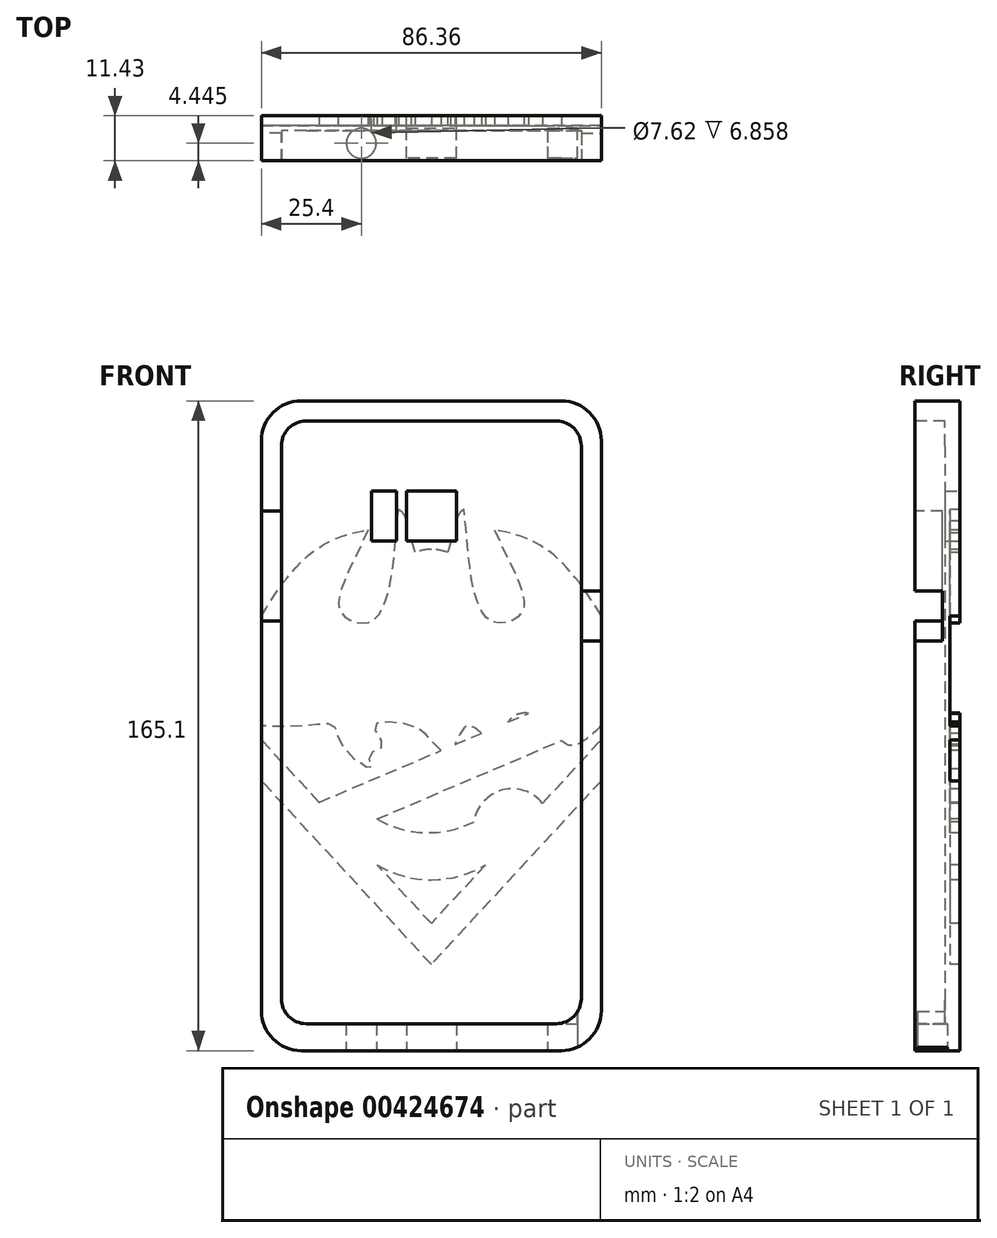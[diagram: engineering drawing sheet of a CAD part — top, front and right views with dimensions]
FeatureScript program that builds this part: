
annotation { "Feature Type Name" : "Feature", "Feature Type Description" : "" }
export const myFeature = defineFeature(function(context is Context, id is Id, definition is map)
    precondition{}
    {
        {
            var Q0;
            Q0=qCreatedBy(makeId("Front.planeOp"),FACE);
            var sketch = newSketch(context, id + "F0", { "sketchPlane" : qUnion([Q0])});
            skLineSegment(sketch, "E0", {"start": v(0, 0) * mm, "end": v(0, -82.55) * mm});
            skLineSegment(sketch, "E1", {"start": v(0, 0) * mm, "end": v(0, 82.55) * mm});
            skLineSegment(sketch, "E2", {"start": v(0, 82.55) * mm, "end": v(-43.18, 82.55) * mm});
            skLineSegment(sketch, "E3", {"start": v(0, 82.55) * mm, "end": v(43.18, 82.55) * mm});
            skLineSegment(sketch, "E4", {"start": v(43.18, 82.55) * mm, "end": v(43.18, -82.55) * mm});
            skLineSegment(sketch, "E5", {"start": v(43.18, -82.55) * mm, "end": v(-43.18, -82.55) * mm});
            skLineSegment(sketch, "E6", {"start": v(-43.18, -82.55) * mm, "end": v(-43.18, 82.55) * mm});
            skSolve(sketch);
        }
        {
            var Q0;
            Q0 = qSketchRegion(id + "F0", true);
            extrude(context, id + "F1", {"entities" : qUnion([Q0]), "depth" : 8.9 * mm});
        }
        {
            var Q0;
            Q0=makeQuery(id+"F1.opExtrude","CAP_FACE",FACE,{"disambiguationData":[OSD([sQuery(id+"F0.wireOp",EDGE,"E2"),sQuery(id+"F0.wireOp",EDGE,"E3"),sQuery(id+"F0.wireOp",EDGE,"E4"),sQuery(id+"F0.wireOp",EDGE,"E5"),sQuery(id+"F0.wireOp",EDGE,"E6")])],"isStart":false});
            var sketch = newSketch(context, id + "F2", { "sketchPlane" : qUnion([Q0])});
            skLineSegment(sketch, "E7", {"start": v(0, 0) * mm, "end": v(0, 77.47) * mm});
            skLineSegment(sketch, "E8", {"start": v(0, 77.47) * mm, "end": v(-38.1, 77.47) * mm});
            skLineSegment(sketch, "E9", {"start": v(-38.1, 77.47) * mm, "end": v(-38.1, -75.7) * mm});
            skLineSegment(sketch, "E10", {"start": v(-38.1, -75.7) * mm, "end": v(38.1, -75.7) * mm});
            skLineSegment(sketch, "E11", {"start": v(38.1, -75.7) * mm, "end": v(38.1, 77.47) * mm});
            skLineSegment(sketch, "E12", {"start": v(38.1, 77.47) * mm, "end": v(0, 77.47) * mm});
            skSolve(sketch);
        }
        {
            var Q0;
            Q0 = qSketchRegion(id + "F2", true);
            extrude(context, id + "F3", {"entities" : qUnion([Q0]), "operationType" : NewBodyOperationType.REMOVE, "oppositeDirection" : true, "depth" : 7.62 * mm});
        }
        {
            var Q0;
            Q0=makeQuery(id+"F1.opExtrude","CAP_FACE",FACE,{"disambiguationData":[OSD([sQuery(id+"F0.wireOp",EDGE,"E2"),sQuery(id+"F0.wireOp",EDGE,"E3"),sQuery(id+"F0.wireOp",EDGE,"E4"),sQuery(id+"F0.wireOp",EDGE,"E5"),sQuery(id+"F0.wireOp",EDGE,"E6")])],"isStart":true});
            var sketch = newSketch(context, id + "F4", { "sketchPlane" : qUnion([Q0])});
            skPoint(sketch, "E13.5.internal.snap0", {"position": v(-43.18, 0) * mm});
            skFitSpline(sketch, "E13", {"points": [v(-43.18, 0) * mm, v(-34.96, -4.96) * mm, v(-28.13, 1.65) * mm, v(-20.27, 1.86) * mm, v(-15.93, -4.14) * mm, v(-9.3, 0) * mm, v(-4.55, -6.62) * mm, v(0, -3.72) * mm, v(4.96, 0) * mm, v(14.48, 0) * mm, v(12.41, -5.17) * mm, v(15.72, -7.45) * mm, v(15.3, -10.76) * mm, v(22.55, -5.17) * mm, v(24.82, 0) * mm, v(32.27, 0) * mm, v(43.18, 0) * mm], "startDerivative": vector(124.68, -118.1) * mm, "endDerivative": vector(115.37, 9.28) * mm});
            skLineSegment(sketch, "E14", {"start": v(-43.18, -13.97) * mm, "end": v(0, -60.61) * mm});
            skLineSegment(sketch, "E15", {"start": v(0, -60.61) * mm, "end": v(43.18, -13.97) * mm});
            skLineSegment(sketch, "E16", {"start": v(-43.18, 0) * mm, "end": v(-43.18, 27.94) * mm});
            skFitSpline(sketch, "E17", {"points": [v(-43.18, 27.94) * mm, v(-16.04, 49.74) * mm], "startDerivative": vector(26.52, 44.64) * mm, "endDerivative": vector(34.13, 4.96) * mm});
            skFitSpline(sketch, "E18", {"points": [v(-16.04, 49.74) * mm, v(-22.64, 28.35) * mm, v(-14.69, 26.9) * mm, v(-8.34, 54.91) * mm], "startDerivative": vector(-48.14, -103.23) * mm, "endDerivative": vector(8.54, 81.55) * mm});
            skFitSpline(sketch, "E19", {"points": [v(-8.34, 54.91) * mm, v(-4.14, 44.06) * mm], "startDerivative": vector(6.87, -1.26) * mm, "endDerivative": vector(4.19, -10.82) * mm});
            skFitSpline(sketch, "E20.MirrorCS", {"points": [v(16.04, 49.74) * mm, v(22.64, 28.35) * mm, v(14.69, 26.9) * mm, v(8.34, 54.91) * mm], "startDerivative": vector(48.14, -103.23) * mm, "endDerivative": vector(-8.54, 81.55) * mm});
            skFitSpline(sketch, "E21.MirrorCS", {"points": [v(43.18, 27.94) * mm, v(16.04, 49.74) * mm], "startDerivative": vector(-26.52, 44.64) * mm, "endDerivative": vector(-34.13, 4.96) * mm});
            skFitSpline(sketch, "E22.MirrorCS", {"points": [v(8.34, 54.91) * mm, v(4.14, 44.06) * mm], "startDerivative": vector(-6.87, -1.26) * mm, "endDerivative": vector(-4.19, -10.82) * mm});
            skArc(sketch, "E23", {"start": v(0, 44.82) * mm, "mid": v(-2.1, 44.6) * mm, "end": v(-4.14, 44.06) * mm});
            skArc(sketch, "E24.MirrorCS", {"start": v(0, 44.82) * mm, "mid": v(2.1, 44.6) * mm, "end": v(4.14, 44.06) * mm});
            skLineSegment(sketch, "E25", {"start": v(-38.06, -9.1) * mm, "end": v(0, -50.22) * mm});
            skLineSegment(sketch, "E26", {"start": v(0, -50.22) * mm, "end": v(13.8, -35.3) * mm});
            skLineSegment(sketch, "E27", {"start": v(-38.06, -9.1) * mm, "end": v(-43.18, -3.58) * mm});
            skArc(sketch, "E28", {"start": v(-13.8, -35.3) * mm, "mid": v(0, -39.14) * mm, "end": v(13.8, -35.3) * mm});
            skArc(sketch, "E29", {"start": v(-10.83, -24.39) * mm, "mid": v(1.58, -27.16) * mm, "end": v(13.8, -23.69) * mm});
            skLineSegment(sketch, "E30", {"start": v(13.8, -23.69) * mm, "end": v(-33.1, -3.76) * mm});
            skLineSegment(sketch, "E31", {"start": v(28.5, -19.44) * mm, "end": v(-2.53, -6.26) * mm});
            skLineSegment(sketch, "E32", {"start": v(-5.97, -4.8) * mm, "end": v(-12.7, -1.94) * mm});
            skLineSegment(sketch, "E33", {"start": v(-19.55, 0.97) * mm, "end": v(-24.66, 3.14) * mm});
            skLineSegment(sketch, "E34", {"start": v(28.5, -19.44) * mm, "end": v(43.18, -3.58) * mm});
            skArc(sketch, "E35", {"start": v(-10.83, -24.39) * mm, "mid": v(-18.01, -16.36) * mm, "end": v(-28.26, -19.7) * mm});
            skSolve(sketch);
        }
        {
            var Q0;
            Q0=makeQuery(id+"F1.opExtrude","SWEPT_FACE",FACE,{"disambiguationData":[OSD([sQuery(id+"F0.wireOp",EDGE,"E5")])]});
            var sketch = newSketch(context, id + "F5", { "sketchPlane" : qUnion([Q0])});
            skLineSegment(sketch, "E36", {"start": v(-43.18, 4.45) * mm, "end": v(-38.1, 4.45) * mm});
            skLineSegment(sketch, "E37", {"start": v(-38.1, 4.45) * mm, "end": v(-38.1, 8.89) * mm});
            skLineSegment(sketch, "E38", {"start": v(-38.1, 8.89) * mm, "end": v(-38.1, 0) * mm});
            skLineSegment(sketch, "E39", {"start": v(43.18, 4.45) * mm, "end": v(38.1, 4.45) * mm});
            skLineSegment(sketch, "E40", {"start": v(38.1, 4.45) * mm, "end": v(38.1, 8.9) * mm});
            skLineSegment(sketch, "E41", {"start": v(38.1, 8.9) * mm, "end": v(38.1, 0) * mm});
            skLineSegment(sketch, "E42", {"start": v(6.35, 4.45) * mm, "end": v(6.35, 0.64) * mm});
            skLineSegment(sketch, "E43", {"start": v(6.35, 4.45) * mm, "end": v(6.35, 8.26) * mm});
            skLineSegment(sketch, "E44", {"start": v(6.35, 8.26) * mm, "end": v(-6.35, 8.26) * mm});
            skLineSegment(sketch, "E45", {"start": v(-6.35, 8.26) * mm, "end": v(-6.35, 0.64) * mm});
            skLineSegment(sketch, "E46", {"start": v(-6.35, 0.64) * mm, "end": v(6.35, 0.64) * mm});
            skCircle(sketch, "E47", {"center": v(-17.78, 4.45) * mm, "radius": 3.81 * mm});
            skLineSegment(sketch, "E48", {"start": v(16.42, 4.45) * mm, "end": v(16.42, 8.26) * mm});
            skLineSegment(sketch, "E49", {"start": v(16.42, 8.26) * mm, "end": v(16.42, 4.45) * mm});
            skLineSegment(sketch, "E50", {"start": v(16.42, 4.45) * mm, "end": v(16.42, 0.64) * mm});
            skLineSegment(sketch, "E51", {"start": v(16.42, 0.64) * mm, "end": v(26.58, 0.64) * mm});
            skLineSegment(sketch, "E52", {"start": v(26.58, 0.64) * mm, "end": v(26.58, 8.26) * mm});
            skLineSegment(sketch, "E53", {"start": v(26.58, 8.26) * mm, "end": v(16.42, 8.26) * mm});
            skLineSegment(sketch, "E54", {"start": v(29.57, 4.45) * mm, "end": v(29.57, 8.26) * mm});
            skLineSegment(sketch, "E55", {"start": v(29.57, 4.45) * mm, "end": v(29.57, 0.64) * mm});
            skLineSegment(sketch, "E56", {"start": v(29.57, 0.64) * mm, "end": v(37.19, 0.64) * mm});
            skLineSegment(sketch, "E57", {"start": v(37.19, 0.64) * mm, "end": v(37.19, 8.26) * mm});
            skLineSegment(sketch, "E58", {"start": v(37.19, 8.26) * mm, "end": v(29.57, 8.26) * mm});
            skLineSegment(sketch, "E59", {"start": v(-38.1, 0) * mm, "end": v(-38.1, 8.9) * mm});
            skLineSegment(sketch, "E60", {"start": v(-38.1, 0) * mm, "end": v(38.1, 0) * mm});
            skSolve(sketch);
        }
        {
            var Q0;
            Q0=makeQuery(id+"F5.imprint","IMPRINT",FACE,{"disambiguationData":[TD([[makeQuery(id+"F5.imprint","IMPRINT",EDGE,{"derivedFrom":sQuery(id+"F5.wireOp",EDGE,"E47")}),1.0]])]});
            var Q1;
            Q1=makeQuery(id+"F5.imprint","IMPRINT",FACE,{"disambiguationData":[TD([[makeQuery(id+"F5.imprint","IMPRINT",EDGE,{"derivedFrom":sQuery(id+"F5.wireOp",EDGE,"E42")}),-1.0]])]});
            var Q2;
            Q2=makeQuery(id+"F5.imprint","IMPRINT",FACE,{"disambiguationData":[TD([[makeQuery(id+"F5.imprint","IMPRINT",EDGE,{"derivedFrom":sQuery(id+"F5.wireOp",EDGE,"E49")}),1.0]])]});
            var Q3;
            Q3=makeQuery(id+"F5.imprint","IMPRINT",FACE,{"disambiguationData":[TD([[makeQuery(id+"F5.imprint","IMPRINT",EDGE,{"derivedFrom":sQuery(id+"F5.wireOp",EDGE,"E54")}),-1.0]])]});
            extrude(context, id + "F6", {"entities" : qUnion([Q0, Q1, Q2, Q3]), "operationType" : NewBodyOperationType.REMOVE, "oppositeDirection" : true, "depth" : 6.86 * mm});
        }
        {
            var Q0;
            Q0=makeQuery(id+"F1.opExtrude","SWEPT_EDGE",EDGE,{"disambiguationData":[OSD([sQuery(id+"F0.wireOp",EDGE,"E5"),sQuery(id+"F0.wireOp",EDGE,"E6")])]});
            var Q1;
            Q1=makeQuery(id+"F1.opExtrude","SWEPT_EDGE",EDGE,{"disambiguationData":[OSD([sQuery(id+"F0.wireOp",EDGE,"E4"),sQuery(id+"F0.wireOp",EDGE,"E5")])]});
            var Q2;
            Q2=makeQuery(id+"F1.opExtrude","SWEPT_EDGE",EDGE,{"disambiguationData":[OSD([sQuery(id+"F0.wireOp",EDGE,"E3"),sQuery(id+"F0.wireOp",EDGE,"E4")])]});
            var Q3;
            Q3=makeQuery(id+"F1.opExtrude","SWEPT_EDGE",EDGE,{"disambiguationData":[OSD([sQuery(id+"F0.wireOp",EDGE,"E2"),sQuery(id+"F0.wireOp",EDGE,"E6")])]});
            fillet(context, id + "F7", {"entities" : qUnion([Q0, Q1, Q2, Q3]), "radius" : 10.16 * mm, "tangentPropagation" : true, "allowEdgeOverflow" : false});
        }
        {
            var Q0;
            Q0=makeQuery(id+"F3.boolean.opBoolean","COPY",EDGE,{"derivedFrom":makeQuery(id+"F3.opExtrude","SWEPT_EDGE",EDGE,{"disambiguationData":[OSD([sQuery(id+"F2.wireOp",EDGE,"E9"),sQuery(id+"F2.wireOp",EDGE,"E10")])]})});
            var Q1;
            Q1=makeQuery(id+"F3.boolean.opBoolean","COPY",EDGE,{"derivedFrom":makeQuery(id+"F3.opExtrude","SWEPT_EDGE",EDGE,{"disambiguationData":[OSD([sQuery(id+"F2.wireOp",EDGE,"E10"),sQuery(id+"F2.wireOp",EDGE,"E11")])]})});
            var Q2;
            Q2=makeQuery(id+"F3.boolean.opBoolean","COPY",EDGE,{"derivedFrom":makeQuery(id+"F3.opExtrude","SWEPT_EDGE",EDGE,{"disambiguationData":[OSD([sQuery(id+"F2.wireOp",EDGE,"E8"),sQuery(id+"F2.wireOp",EDGE,"E9")])]})});
            var Q3;
            Q3=makeQuery(id+"F3.boolean.opBoolean","COPY",EDGE,{"derivedFrom":makeQuery(id+"F3.opExtrude","SWEPT_EDGE",EDGE,{"disambiguationData":[OSD([sQuery(id+"F2.wireOp",EDGE,"E11"),sQuery(id+"F2.wireOp",EDGE,"E12")])]})});
            fillet(context, id + "F8", {"entities" : qUnion([Q0, Q1, Q2, Q3]), "radius" : 6.35 * mm, "tangentPropagation" : true, "allowEdgeOverflow" : false});
        }
        {
            var Q0;
            Q0=makeQuery(id+"F1.opExtrude","SWEPT_FACE",FACE,{"disambiguationData":[OSD([sQuery(id+"F0.wireOp",EDGE,"E4")])]});
            var sketch = newSketch(context, id + "F9", { "sketchPlane" : qUnion([Q0])});
            skLineSegment(sketch, "E61", {"start": v(-4.45, 21.6) * mm, "end": v(-6.99, 21.6) * mm});
            skLineSegment(sketch, "E62", {"start": v(-6.99, 21.6) * mm, "end": v(-6.99, 34.3) * mm});
            skLineSegment(sketch, "E63", {"start": v(-6.99, 34.3) * mm, "end": v(-1.9, 34.3) * mm});
            skLineSegment(sketch, "E64", {"start": v(-1.9, 34.3) * mm, "end": v(-1.9, 21.6) * mm});
            skLineSegment(sketch, "E65", {"start": v(-1.9, 21.6) * mm, "end": v(-4.45, 21.6) * mm});
            skSolve(sketch);
        }
        {
            var Q0;
            Q0=makeQuery(id+"F9.imprint","IMPRINT",FACE,{"disambiguationData":[TD([[makeQuery(id+"F9.imprint","IMPRINT",EDGE,{"derivedFrom":sQuery(id+"F9.wireOp",EDGE,"E61")}),-1.0]])]});
            extrude(context, id + "F10", {"entities" : qUnion([Q0]), "operationType" : NewBodyOperationType.REMOVE, "oppositeDirection" : true, "depth" : 25.4 * mm});
        }
        {
            var Q0;
            Q0=makeQuery(id+"F1.opExtrude","SWEPT_FACE",FACE,{"disambiguationData":[OSD([sQuery(id+"F0.wireOp",EDGE,"E6")])]});
            var sketch = newSketch(context, id + "F11", { "sketchPlane" : qUnion([Q0])});
            skLineSegment(sketch, "E66", {"start": v(4.45, 26.67) * mm, "end": v(1.9, 26.67) * mm});
            skLineSegment(sketch, "E67", {"start": v(1.9, 26.67) * mm, "end": v(1.9, 39.37) * mm});
            skLineSegment(sketch, "E68", {"start": v(1.9, 39.37) * mm, "end": v(6.99, 39.37) * mm});
            skLineSegment(sketch, "E69", {"start": v(6.99, 39.37) * mm, "end": v(6.99, 26.67) * mm});
            skLineSegment(sketch, "E70", {"start": v(6.99, 26.67) * mm, "end": v(4.45, 26.67) * mm});
            skLineSegment(sketch, "E71", {"start": v(4.44, 41.9) * mm, "end": v(1.9, 41.9) * mm});
            skLineSegment(sketch, "E72", {"start": v(1.9, 41.9) * mm, "end": v(1.9, 54.6) * mm});
            skLineSegment(sketch, "E73", {"start": v(1.9, 54.6) * mm, "end": v(6.99, 54.6) * mm});
            skLineSegment(sketch, "E74", {"start": v(6.99, 54.6) * mm, "end": v(6.99, 41.9) * mm});
            skLineSegment(sketch, "E75", {"start": v(6.99, 41.9) * mm, "end": v(4.44, 41.9) * mm});
            skSolve(sketch);
        }
        {
            var Q0;
            Q0 = qSketchRegion(id + "F11", true);
            extrude(context, id + "F12", {"entities" : qUnion([Q0]), "operationType" : NewBodyOperationType.REMOVE, "oppositeDirection" : true, "depth" : 25.4 * mm});
        }
        {
            var Q0;
            {var subQ1=sQuery(id+"F4.wireOp",EDGE,"E17");Q0=makeQuery(id+"F4.imprint","IMPRINT",FACE,{"disambiguationData":[TD([[makeQuery(id+"F4.imprint","IMPRINT",EDGE,{"derivedFrom":subQ1}),1.0]])]});}
            var sketch = newSketch(context, id + "F13", { "sketchPlane" : qUnion([Q0])});
            skLineSegment(sketch, "E76.0", {"start": v(-38.1, 77.47) * mm, "end": v(0, 77.47) * mm});
            skLineSegment(sketch, "E77.0", {"start": v(0, 77.47) * mm, "end": v(38.1, 77.47) * mm});
            skLineSegment(sketch, "E78", {"start": v(0, 77.47) * mm, "end": v(0, 47) * mm});
            skLineSegment(sketch, "E79", {"start": v(0, 47) * mm, "end": v(-6.35, 47) * mm});
            skLineSegment(sketch, "E80", {"start": v(-6.35, 47) * mm, "end": v(-6.35, 59.7) * mm});
            skLineSegment(sketch, "E81", {"start": v(-6.35, 59.7) * mm, "end": v(6.35, 59.7) * mm});
            skLineSegment(sketch, "E82", {"start": v(6.35, 59.7) * mm, "end": v(6.35, 47) * mm});
            skLineSegment(sketch, "E83", {"start": v(6.35, 47) * mm, "end": v(0, 47) * mm});
            skLineSegment(sketch, "E84", {"start": v(8.89, 59.7) * mm, "end": v(15.24, 59.7) * mm});
            skLineSegment(sketch, "E85", {"start": v(15.24, 59.7) * mm, "end": v(15.24, 47) * mm});
            skLineSegment(sketch, "E86", {"start": v(15.24, 47) * mm, "end": v(8.9, 47) * mm});
            skLineSegment(sketch, "E87", {"start": v(8.9, 47) * mm, "end": v(8.89, 59.7) * mm});
            skSolve(sketch);
        }
        {
            var Q0;
            Q0 = qSketchRegion(id + "F13", true);
            extrude(context, id + "F14", {"entities" : qUnion([Q0]), "operationType" : NewBodyOperationType.REMOVE, "oppositeDirection" : true, "depth" : 25.4 * mm});
        }
        {
            var Q0;
            {var subQ1=sQuery(id+"F4.wireOp",EDGE,"E17");Q0=makeQuery(id+"F4.imprint","IMPRINT",FACE,{"disambiguationData":[TD([[makeQuery(id+"F4.imprint","IMPRINT",EDGE,{"derivedFrom":subQ1}),1.0]])]});}
            var Q1;
            {var subQ2=sQuery(id+"F4.wireOp",EDGE,"E14");Q1=makeQuery(id+"F4.imprint","IMPRINT",FACE,{"disambiguationData":[TD([[makeQuery(id+"F4.imprint","IMPRINT",EDGE,{"derivedFrom":subQ2}),-1.0]])]});}
            extrude(context, id + "F15", {"entities" : qUnion([Q0, Q1]), "operationType" : NewBodyOperationType.ADD, "depth" : 2.54 * mm});
        }
        {
            var Q0;
            Q0=makeQuery(id+"F15.opExtrude","SWEPT_EDGE",EDGE,{"disambiguationData":[OSD([sQuery(id+"F0.wireOp",EDGE,"E2"),sQuery(id+"F0.wireOp",EDGE,"E3"),sQuery(id+"F0.wireOp",EDGE,"E4")])]});
            var Q1;
            Q1=makeQuery(id+"F15.opExtrude","SWEPT_EDGE",EDGE,{"disambiguationData":[OSD([sQuery(id+"F0.wireOp",EDGE,"E2"),sQuery(id+"F0.wireOp",EDGE,"E3"),sQuery(id+"F0.wireOp",EDGE,"E6")])]});
            var Q2;
            Q2=makeQuery(id+"F15.opExtrude","SWEPT_EDGE",EDGE,{"disambiguationData":[OSD([sQuery(id+"F0.wireOp",EDGE,"E5"),sQuery(id+"F0.wireOp",EDGE,"E6")])]});
            var Q3;
            Q3=makeQuery(id+"F15.opExtrude","SWEPT_EDGE",EDGE,{"disambiguationData":[OSD([sQuery(id+"F0.wireOp",EDGE,"E4"),sQuery(id+"F0.wireOp",EDGE,"E5")])]});
            fillet(context, id + "F16", {"entities" : qUnion([Q0, Q1, Q2, Q3]), "radius" : 10.16 * mm, "tangentPropagation" : true, "allowEdgeOverflow" : false});
        }
        {
            var Q0;
            {var subQ0=sQuery(id+"F4.wireOp",EDGE,"E27");Q0=makeQuery(id+"F4.imprint","IMPRINT",FACE,{"disambiguationData":[TD([[makeQuery(id+"F4.imprint","IMPRINT",EDGE,{"derivedFrom":subQ0}),-1.0]])]});}
            var Q1;
            {var subQ0=sQuery(id+"F4.wireOp",EDGE,"E26");Q1=makeQuery(id+"F4.imprint","IMPRINT",FACE,{"disambiguationData":[TD([[makeQuery(id+"F4.imprint","IMPRINT",EDGE,{"derivedFrom":subQ0}),1.0]])]});}
            var Q2;
            {var subQ3=sQuery(id+"F4.wireOp",EDGE,"E31");Q2=makeQuery(id+"F4.imprint","IMPRINT",FACE,{"disambiguationData":[TD([[makeQuery(id+"F4.imprint","IMPRINT",EDGE,{"derivedFrom":subQ3}),-1.0]])]});}
            var Q3;
            {var subQ0=sQuery(id+"F4.wireOp",EDGE,"E32");Q3=makeQuery(id+"F4.imprint","IMPRINT",FACE,{"disambiguationData":[TD([[makeQuery(id+"F4.imprint","IMPRINT",EDGE,{"derivedFrom":subQ0}),-1.0]])]});}
            var Q4;
            {var subQ0=sQuery(id+"F4.wireOp",EDGE,"E33");Q4=makeQuery(id+"F4.imprint","IMPRINT",FACE,{"disambiguationData":[TD([[makeQuery(id+"F4.imprint","IMPRINT",EDGE,{"derivedFrom":subQ0}),-1.0]])]});}
            extrude(context, id + "F17", {"entities" : qUnion([Q0, Q1, Q2, Q3, Q4]), "operationType" : NewBodyOperationType.ADD, "depth" : 2.54 * mm});
        }
        {
            var Q0;
            Q0=makeQuery(id+"F15.opExtrude","CAP_FACE",FACE,{"disambiguationData":[OSD([sQuery(id+"F0.wireOp",EDGE,"E2"),sQuery(id+"F0.wireOp",EDGE,"E3"),sQuery(id+"F0.wireOp",EDGE,"E4"),sQuery(id+"F0.wireOp",EDGE,"E6"),sQuery(id+"F4.wireOp",EDGE,"E17"),sQuery(id+"F4.wireOp",EDGE,"E18"),sQuery(id+"F4.wireOp",EDGE,"E19"),sQuery(id+"F4.wireOp",EDGE,"E20.MirrorCS"),sQuery(id+"F4.wireOp",EDGE,"E21.MirrorCS"),sQuery(id+"F4.wireOp",EDGE,"E22.MirrorCS"),sQuery(id+"F4.wireOp",EDGE,"E23"),sQuery(id+"F4.wireOp",EDGE,"E24.MirrorCS")])],"isStart":false});
            var sketch = newSketch(context, id + "F18", { "sketchPlane" : qUnion([Q0])});
            skLineSegment(sketch, "E88.0", {"start": v(0, 47) * mm, "end": v(-6.35, 47) * mm});
            skLineSegment(sketch, "E89.0", {"start": v(6.35, 47) * mm, "end": v(0, 47) * mm});
            skLineSegment(sketch, "E90.0", {"start": v(-6.35, 47) * mm, "end": v(-6.35, 59.7) * mm});
            skLineSegment(sketch, "E91.0", {"start": v(6.35, 59.7) * mm, "end": v(6.35, 47) * mm});
            skLineSegment(sketch, "E92.0", {"start": v(-6.35, 59.7) * mm, "end": v(6.35, 59.7) * mm});
            skLineSegment(sketch, "E93.0", {"start": v(8.9, 47) * mm, "end": v(8.89, 59.7) * mm});
            skLineSegment(sketch, "E94.0", {"start": v(8.89, 59.7) * mm, "end": v(15.24, 59.7) * mm});
            skLineSegment(sketch, "E95.0", {"start": v(15.24, 59.7) * mm, "end": v(15.24, 47) * mm});
            skPoint(sketch, "E96.0", {"position": v(12.07, 47) * mm});
            skLineSegment(sketch, "E97.0", {"start": v(15.24, 47) * mm, "end": v(8.9, 47) * mm});
            skSolve(sketch);
        }
        {
            var Q0;
            {var subQ0=sQuery(id+"F18.wireOp",EDGE,"E92.0");Q0=makeQuery(id+"F18.imprint","IMPRINT",FACE,{"disambiguationData":[TD([[makeQuery(id+"F18.imprint","IMPRINT",EDGE,{"derivedFrom":subQ0}),-1.0]])]});}
            var Q1;
            {var subQ4=sQuery(id+"F18.wireOp",EDGE,"E94.0");Q1=makeQuery(id+"F18.imprint","IMPRINT",FACE,{"disambiguationData":[TD([[makeQuery(id+"F18.imprint","IMPRINT",EDGE,{"derivedFrom":subQ4}),-1.0]])]});}
            extrude(context, id + "F19", {"entities" : qUnion([Q0, Q1]), "operationType" : NewBodyOperationType.REMOVE, "endBound" : BoundingType.THROUGH_ALL, "oppositeDirection" : true, "depth" : 25.4 * mm});
        }
        {
            var Q0;
            Q0=makeQuery(id+"F9.imprint","IMPRINT",FACE,{"disambiguationData":[TD([[makeQuery(id+"F9.imprint","IMPRINT",EDGE,{"derivedFrom":sQuery(id+"F9.wireOp",EDGE,"E61")}),1.0]])]});
            var sketch = newSketch(context, id + "F20", { "sketchPlane" : qUnion([Q0])});
            skLineSegment(sketch, "E98.0", {"start": v(-6.99, 21.6) * mm, "end": v(-6.99, 34.3) * mm});
            skLineSegment(sketch, "E99", {"start": v(-6.99, 21.6) * mm, "end": v(-9.5, 21.6) * mm});
            skLineSegment(sketch, "E100", {"start": v(-9.5, 21.6) * mm, "end": v(-9.5, 34.3) * mm});
            skLineSegment(sketch, "E101", {"start": v(-9.5, 34.3) * mm, "end": v(-6.99, 34.3) * mm});
            skSolve(sketch);
        }
        {
            var Q0;
            Q0 = qSketchRegion(id + "F20", true);
            extrude(context, id + "F21", {"entities" : qUnion([Q0]), "operationType" : NewBodyOperationType.REMOVE, "oppositeDirection" : true, "depth" : 12.7 * mm});
        }
        {
            var Q0;
            Q0=makeQuery(id+"F11.imprint","IMPRINT",FACE,{"disambiguationData":[TD([[makeQuery(id+"F11.imprint","IMPRINT",EDGE,{"derivedFrom":sQuery(id+"F11.wireOp",EDGE,"E66")}),1.0]])]});
            var sketch = newSketch(context, id + "F22", { "sketchPlane" : qUnion([Q0])});
            skLineSegment(sketch, "E102.0", {"start": v(6.99, 39.37) * mm, "end": v(6.99, 26.67) * mm});
            skLineSegment(sketch, "E103.0", {"start": v(6.99, 54.6) * mm, "end": v(6.99, 41.9) * mm});
            skLineSegment(sketch, "E104", {"start": v(6.99, 54.6) * mm, "end": v(11.18, 54.6) * mm});
            skLineSegment(sketch, "E105", {"start": v(11.18, 54.6) * mm, "end": v(11.18, 26.67) * mm});
            skLineSegment(sketch, "E106", {"start": v(11.18, 26.67) * mm, "end": v(6.99, 26.67) * mm});
            skLineSegment(sketch, "E107", {"start": v(6.99, 39.37) * mm, "end": v(6.99, 41.9) * mm});
            skSolve(sketch);
        }
        {
            var Q0;
            Q0 = qSketchRegion(id + "F22", true);
            extrude(context, id + "F23", {"entities" : qUnion([Q0]), "operationType" : NewBodyOperationType.REMOVE, "oppositeDirection" : true, "depth" : 12.7 * mm});
        }
        {
            var Q0;
            Q0=makeQuery(id+"F11.imprint","IMPRINT",FACE,{"disambiguationData":[TD([[makeQuery(id+"F11.imprint","IMPRINT",EDGE,{"derivedFrom":sQuery(id+"F11.wireOp",EDGE,"E66")}),1.0]])]});
            var sketch = newSketch(context, id + "F24", { "sketchPlane" : qUnion([Q0])});
            skLineSegment(sketch, "E108.0", {"start": v(1.9, 39.37) * mm, "end": v(6.99, 39.37) * mm});
            skPoint(sketch, "E109.0", {"position": v(3.17, 41.9) * mm});
            skLineSegment(sketch, "E110.0", {"start": v(4.44, 41.9) * mm, "end": v(1.9, 41.9) * mm});
            skPoint(sketch, "E111.0", {"position": v(5.72, 41.9) * mm});
            skLineSegment(sketch, "E112.0", {"start": v(6.99, 41.9) * mm, "end": v(4.44, 41.9) * mm});
            skLineSegment(sketch, "E113.0", {"start": v(6.99, 39.37) * mm, "end": v(6.99, 41.9) * mm});
            skLineSegment(sketch, "E114", {"start": v(1.9, 41.9) * mm, "end": v(1.9, 39.37) * mm});
            skSolve(sketch);
        }
        {
            var Q0;
            Q0 = qSketchRegion(id + "F24", true);
            extrude(context, id + "F25", {"entities" : qUnion([Q0]), "operationType" : NewBodyOperationType.REMOVE, "oppositeDirection" : true, "depth" : 12.7 * mm});
        }
    });
